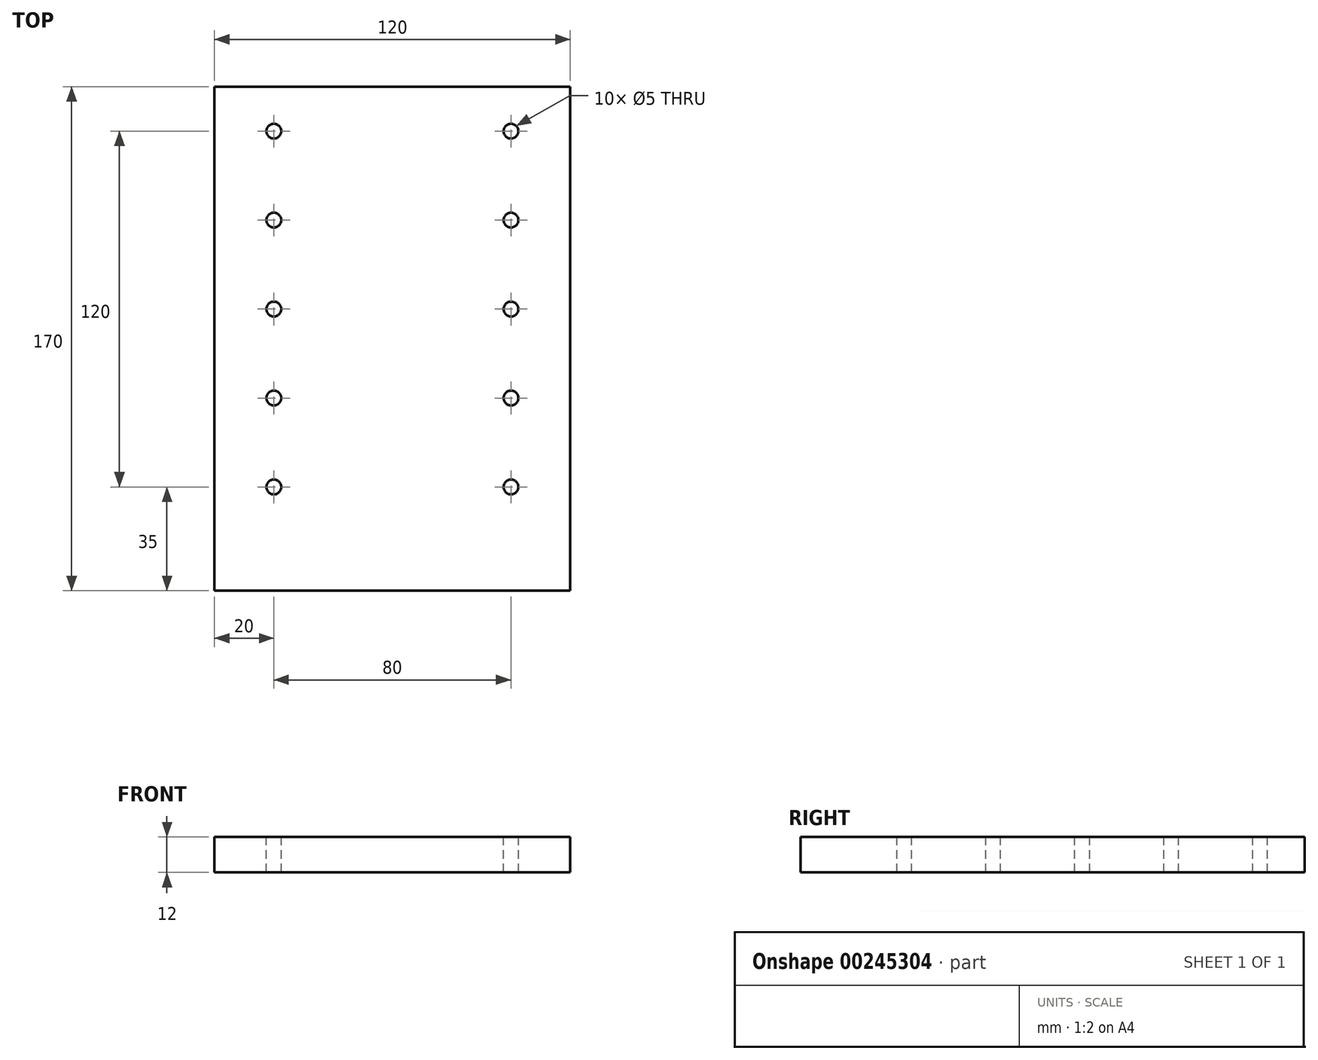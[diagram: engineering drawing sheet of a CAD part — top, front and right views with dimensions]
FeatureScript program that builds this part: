
annotation { "Feature Type Name" : "Feature", "Feature Type Description" : "" }
export const myFeature = defineFeature(function(context is Context, id is Id, definition is map)
    precondition{}
    {
        {
            var Q0;
            Q0=qCreatedBy(makeId("Front.planeOp"),FACE);
            var sketch = newSketch(context, id + "F0", { "sketchPlane" : qUnion([Q0])});
            skLineSegment(sketch, "E0.bottom", {"start": v(0, 0) * mm, "end": v(120, 0) * mm});
            skLineSegment(sketch, "E0.top", {"start": v(0, 12) * mm, "end": v(120, 12) * mm});
            skLineSegment(sketch, "E0.left", {"start": v(0, 0) * mm, "end": v(0, 12) * mm});
            skLineSegment(sketch, "E0.right", {"start": v(120, 0) * mm, "end": v(120, 12) * mm});
            skLineSegment(sketch, "E1.bottom", {"start": v(0, 12) * mm, "end": v(66.98, 12) * mm});
            skSolve(sketch);
        }
        {
            var Q0;
            Q0=makeQuery(id+"F0.imprint","IMPRINT",FACE,{"disambiguationData":[TD([[makeQuery(id+"F0.imprint","IMPRINT",EDGE,{"derivedFrom":sQuery(id+"F0.wireOp",EDGE,"E0.bottom")}),1.0]])]});
            extrude(context, id + "F1", {"entities" : qUnion([Q0]), "depth" : 170 * mm});
        }
        {
            var Q0;
            Q0=makeQuery(id+"F1.opExtrude","SWEPT_FACE",FACE,{"disambiguationData":[OSD([sQuery(id+"F0.wireOp",EDGE,"E0.top"),sQuery(id+"F0.wireOp",EDGE,"E1.bottom")])]});
            var sketch = newSketch(context, id + "F2", { "sketchPlane" : qUnion([Q0])});
            skPoint(sketch, "E2", {"position": v(20, -15) * mm});
            skPoint(sketch, "E3", {"position": v(20, -45) * mm});
            skPoint(sketch, "E4", {"position": v(20, -75) * mm});
            skPoint(sketch, "E5", {"position": v(20, -105) * mm});
            skPoint(sketch, "E6", {"position": v(20, -135) * mm});
            skSolve(sketch);
        }
        {
            var Q0;
            Q0=sQuery(id+"F2.wireOp",VERTEX,"E2");
            var Q1;
            Q1=sQuery(id+"F2.wireOp",VERTEX,"E3");
            var Q2;
            Q2=sQuery(id+"F2.wireOp",VERTEX,"E4");
            var Q3;
            Q3=sQuery(id+"F2.wireOp",VERTEX,"E5");
            var Q4;
            Q4=sQuery(id+"F2.wireOp",VERTEX,"E6");
            var Q5;
            Q5=makeQuery(id+"F1.opExtrude","SWEPT_BODY",BODY,{"disambiguationData":[OSD([sQuery(id+"F0.wireOp",EDGE,"E0.bottom"),sQuery(id+"F0.wireOp",EDGE,"E0.top"),sQuery(id+"F0.wireOp",EDGE,"E0.left"),sQuery(id+"F0.wireOp",EDGE,"E0.right"),sQuery(id+"F0.wireOp",EDGE,"E1.bottom")])]});
            hole(context, id + "F3", {"style" : HoleStyle.SIMPLE, "endStyle" : HoleEndStyle.THROUGH, "standardTappedOrClearance" : lookupTablePath({ "standard" : "ISO", "engagement" : "75%", "pitch" : "1 mm", "size" : "M6", "type" : "Tapped" }), "standardBlindInLast" : lookupTablePath({ "standard" : "ISO", "engagement" : "75%", "pitch" : "1 mm", "size" : "M6", "type" : "Tapped" }), "holeDiameter" : 5 * mm, "showTappedDepth" : true, "tappedDepth" : 12 * mm, "tapClearance" : 3, "locations" : qUnion([Q0, Q1, Q2, Q3, Q4]), "scope" : qUnion([Q5]), "majorDiameter" : 6 * mm});
        }
        {
            var Q0;
            Q0=makeQuery(id+"F1.opExtrude","SWEPT_FACE",FACE,{"disambiguationData":[OSD([sQuery(id+"F0.wireOp",EDGE,"E0.top"),sQuery(id+"F0.wireOp",EDGE,"E1.bottom")])]});
            var sketch = newSketch(context, id + "F4", { "sketchPlane" : qUnion([Q0])});
            skPoint(sketch, "E7", {"position": v(100, -15) * mm});
            skPoint(sketch, "E8", {"position": v(100, -45) * mm});
            skPoint(sketch, "E9", {"position": v(100, -75) * mm});
            skPoint(sketch, "E10", {"position": v(100, -105) * mm});
            skPoint(sketch, "E11", {"position": v(100, -135) * mm});
            skSolve(sketch);
        }
        {
            var Q0;
            Q0=sQuery(id+"F4.wireOp",VERTEX,"E7");
            var Q1;
            Q1=sQuery(id+"F4.wireOp",VERTEX,"E8");
            var Q2;
            Q2=sQuery(id+"F4.wireOp",VERTEX,"E9");
            var Q3;
            Q3=sQuery(id+"F4.wireOp",VERTEX,"E10");
            var Q4;
            Q4=sQuery(id+"F4.wireOp",VERTEX,"E11");
            var Q5;
            Q5=makeQuery(id+"F1.opExtrude","SWEPT_BODY",BODY,{"disambiguationData":[OSD([sQuery(id+"F0.wireOp",EDGE,"E0.bottom"),sQuery(id+"F0.wireOp",EDGE,"E0.top"),sQuery(id+"F0.wireOp",EDGE,"E0.left"),sQuery(id+"F0.wireOp",EDGE,"E0.right"),sQuery(id+"F0.wireOp",EDGE,"E1.bottom")])]});
            hole(context, id + "F5", {"style" : HoleStyle.SIMPLE, "endStyle" : HoleEndStyle.THROUGH, "standardTappedOrClearance" : lookupTablePath({ "standard" : "ISO", "engagement" : "75%", "pitch" : "1 mm", "size" : "M6", "type" : "Tapped" }), "standardBlindInLast" : lookupTablePath({ "standard" : "ISO", "engagement" : "75%", "pitch" : "1 mm", "size" : "M6", "type" : "Tapped" }), "holeDiameter" : 5 * mm, "showTappedDepth" : true, "tappedDepth" : 12 * mm, "tapClearance" : 3, "locations" : qUnion([Q0, Q1, Q2, Q3, Q4]), "scope" : qUnion([Q5]), "majorDiameter" : 6 * mm});
        }
    });
